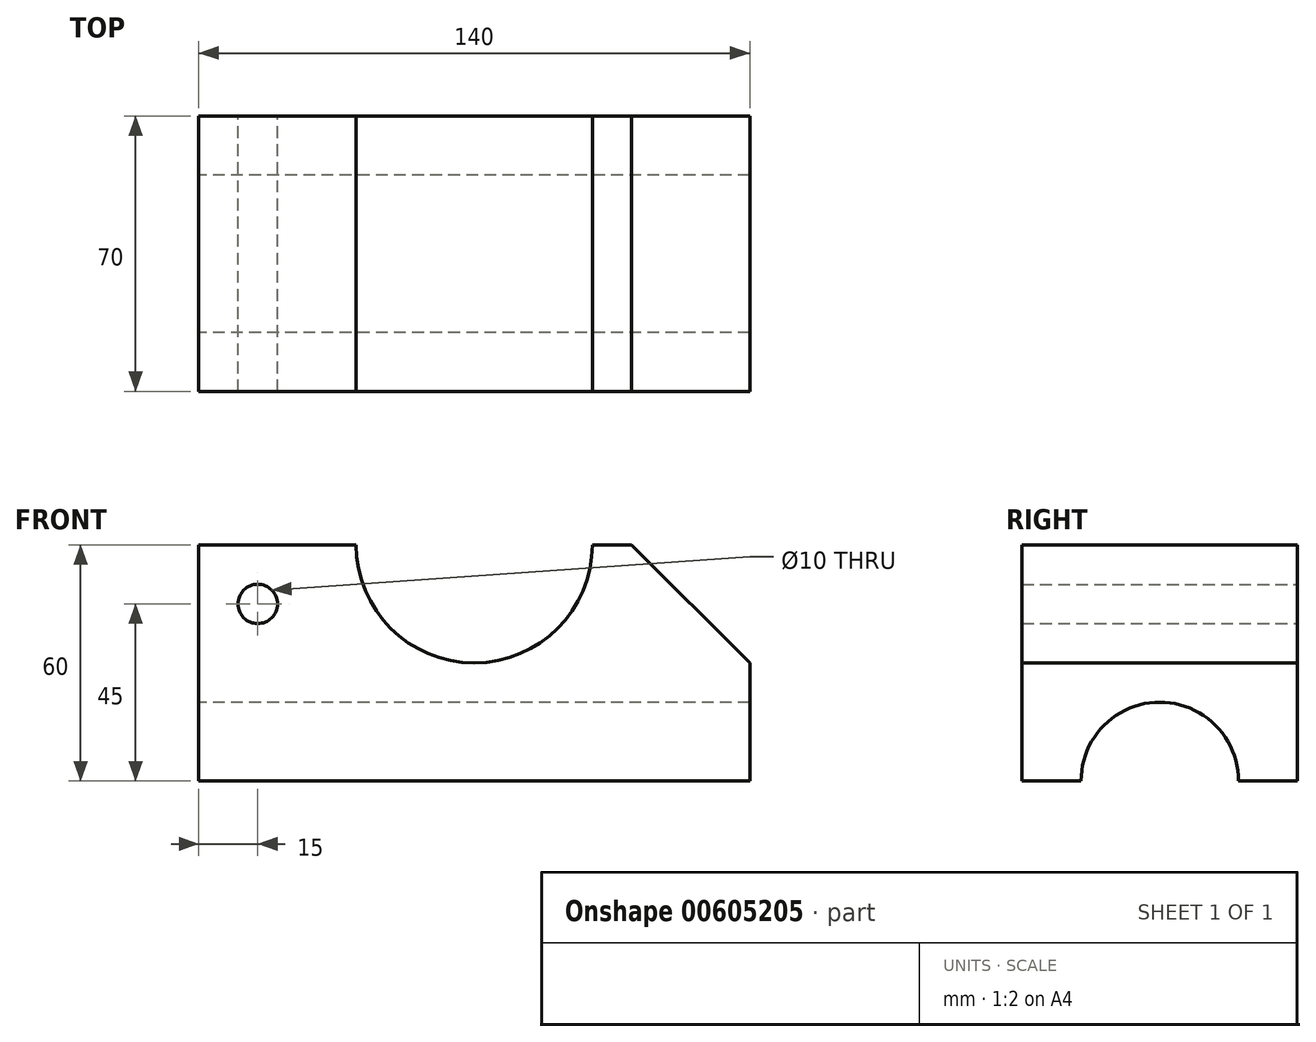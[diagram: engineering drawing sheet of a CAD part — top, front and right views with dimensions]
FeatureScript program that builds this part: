
annotation { "Feature Type Name" : "Feature", "Feature Type Description" : "" }
export const myFeature = defineFeature(function(context is Context, id is Id, definition is map)
    precondition{}
    {
        {
            var Q0;
            Q0=qCreatedBy(makeId("Front.planeOp"),FACE);
            var sketch = newSketch(context, id + "F0", { "sketchPlane" : qUnion([Q0])});
            skLineSegment(sketch, "E0.bottom", {"start": v(70, 30) * mm, "end": v(30, 30) * mm});
            skLineSegment(sketch, "E0.top", {"start": v(70, -30) * mm, "end": v(-70, -30) * mm});
            skLineSegment(sketch, "E0.left", {"start": v(70, 30) * mm, "end": v(70, -30) * mm});
            skLineSegment(sketch, "E0.right", {"start": v(-70, 30) * mm, "end": v(-70, -30) * mm});
            skPoint(sketch, "E0.middle", {"position": v(0, 0) * mm});
            skArc(sketch, "E1", {"start": v(-30, 30) * mm, "mid": v(0, 0) * mm, "end": v(30, 30) * mm});
            skLineSegment(sketch, "E2.trimOffspring", {"start": v(-30, 30) * mm, "end": v(-70, 30) * mm});
            skLineSegment(sketch, "E3", {"start": v(70, 0) * mm, "end": v(40, 0) * mm});
            skLineSegment(sketch, "E4", {"start": v(40, 0) * mm, "end": v(40, 30) * mm});
            skLineSegment(sketch, "E5", {"start": v(-70, 0) * mm, "end": v(-40, 0) * mm});
            skLineSegment(sketch, "E6", {"start": v(-40, 0) * mm, "end": v(-40, 30) * mm});
            skLineSegment(sketch, "E7", {"start": v(40, 30) * mm, "end": v(70, 0) * mm});
            skCircle(sketch, "E8", {"center": v(-55, 15) * mm, "radius": 5 * mm});
            skSolve(sketch);
        }
        {
            var Q0;
            {var subQ4=sQuery(id+"F0.wireOp",EDGE,"E3");Q0=makeQuery(id+"F0.imprint","IMPRINT",FACE,{"disambiguationData":[TD([[makeQuery(id+"F0.imprint","IMPRINT",EDGE,{"derivedFrom":subQ4}),-1.0]])]});}
            var Q1;
            {var subQ3=sQuery(id+"F0.wireOp",EDGE,"E5");Q1=makeQuery(id+"F0.imprint","IMPRINT",FACE,{"disambiguationData":[TD([[makeQuery(id+"F0.imprint","IMPRINT",EDGE,{"derivedFrom":subQ3}),1.0]])]});}
            var Q2;
            {var subQ1=sQuery(id+"F0.wireOp",EDGE,"E0.top");Q2=makeQuery(id+"F0.imprint","IMPRINT",FACE,{"disambiguationData":[TD([[makeQuery(id+"F0.imprint","IMPRINT",EDGE,{"derivedFrom":subQ1}),-1.0]])]});}
            extrude(context, id + "F1", {"entities" : qUnion([Q0, Q1, Q2]), "depth" : 70 * mm, "offsetDistance" : 25 * mm});
        }
        {
            var Q0;
            Q0=qCreatedBy(makeId("Right.planeOp"),FACE);
            var sketch = newSketch(context, id + "F2", { "sketchPlane" : qUnion([Q0])});
            skCircle(sketch, "E9", {"center": v(-35, -29.97) * mm, "radius": 20 * mm});
            skSolve(sketch);
        }
        {
            var Q0;
            Q0=makeQuery(id+"F2.imprint","IMPRINT",FACE,{"disambiguationData":[TD([[makeQuery(id+"F2.imprint","IMPRINT",EDGE,{"derivedFrom":sQuery(id+"F2.wireOp",EDGE,"E9")}),1.0]])]});
            extrude(context, id + "F3", {"entities" : qUnion([Q0]), "operationType" : NewBodyOperationType.REMOVE, "depth" : 140 * mm, "offsetDistance" : 25 * mm, "symmetric" : true});
        }
    });
